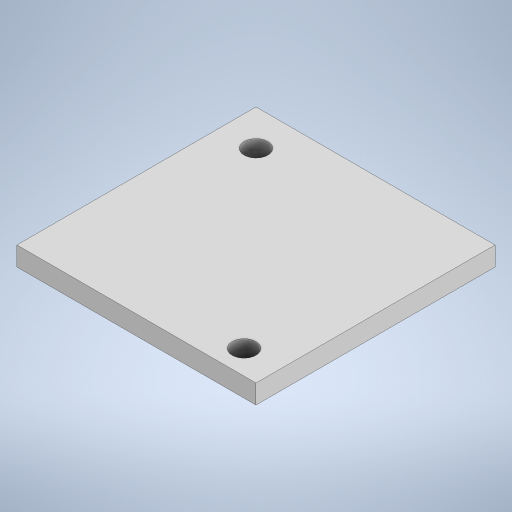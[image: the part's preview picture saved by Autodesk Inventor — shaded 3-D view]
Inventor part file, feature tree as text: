
AUTODESK INVENTOR PART (.ipt)
format: ipt  version: 2023 (Build 270158000, 158)  size: 205,824 bytes
history: native  units: mm
features: other x1, extrude x1, sketch x1
ambient origin geometry x8: Origin, YZ Plane, XZ Plane, XY Plane, X Axis, Y Axis, Z Axis, Center Point
bodies: Body1 (feature_tree)
feature tree (3):
  other  "Bryła1"
  extrude  "Wyciągnięcie proste1"  Depth=20.0mm
  sketch  "Szkic1"
